# Revit family: Sanitary_Showers_hansgrohe_24357USA-hansgrohe-Shower-arm-S-39-cm_new
name_source: partatom
category: Plumbing Fixtures
revit_build: Autodesk Revit 2018 (Build: 20170223_1515(x64)
units: mm (PartAtom-declared; Revit-internal decimal feet)

## family parameters
Always vertical = No
Cut with Voids When Loaded = No
OmniClass Number = 23.31.17.00
OmniClass Title = Showers
Part Type = Normal
Room Calculation Point = No
Round Connector Dimension = Use Diameter
Shared = No
Work Plane-Based = Yes

## types (3) — shared parameters
Always visible = Yes
BIMobject category = Showers
Connector Description = Water Inlet 1/2
Default Elevation = 4' - 0"
Description = hansgrohe Shower arm S 39 cm
Design country = Germany
Diameter = 1"
Edition number = 1
IFC Classification = Sanitary Terminal
Manufacturer = Hansgrohe
Manufacturer country = Germany
Manufacturer name = hansgrohe
Masterformat 2014 Code = 22 41 23
Masterformat 2014 Description = Residential Showers
Model = 24357USA
OmniClass Code = 23-31 17 00
OmniClass Description = Showers
Product Guid = 111f6e8d-1d32-4a3c-a3c9-968940f16aaf
Product SKU = 24357USA
Product data url = https://bimobject.com
Product name = 24357USA hansgrohe Shower arm S 39 cm
Product url = https://www.hansgrohe.com
QR code = https://bimobject.com
UNSPSC Code = 30181503
URL = https://www.hansgrohe.com
Uniclass 2015 Code = Pr_40_20_87_76
Uniclass 2015 Name = Shower heads
Uniformat II Code = D2010
Uniformat II Description = Plumbing Fixtures
Weight Net (Kg) = 1.5

## per-type parameters (varying)
| type | Material 1 |
| 821 Brushed Nickel | Hansgrohe - Metal - 821 Brushed Nickel |
| 671 Matte Black | Hansgrohe - Metal - 671 Matte Black |
| 001 Chrome | Hansgrohe - Metal - 001 Chrome |

## geometry (parser evidence)
native form markers: Sweep x1
no freeform markers — native parametric forms only
